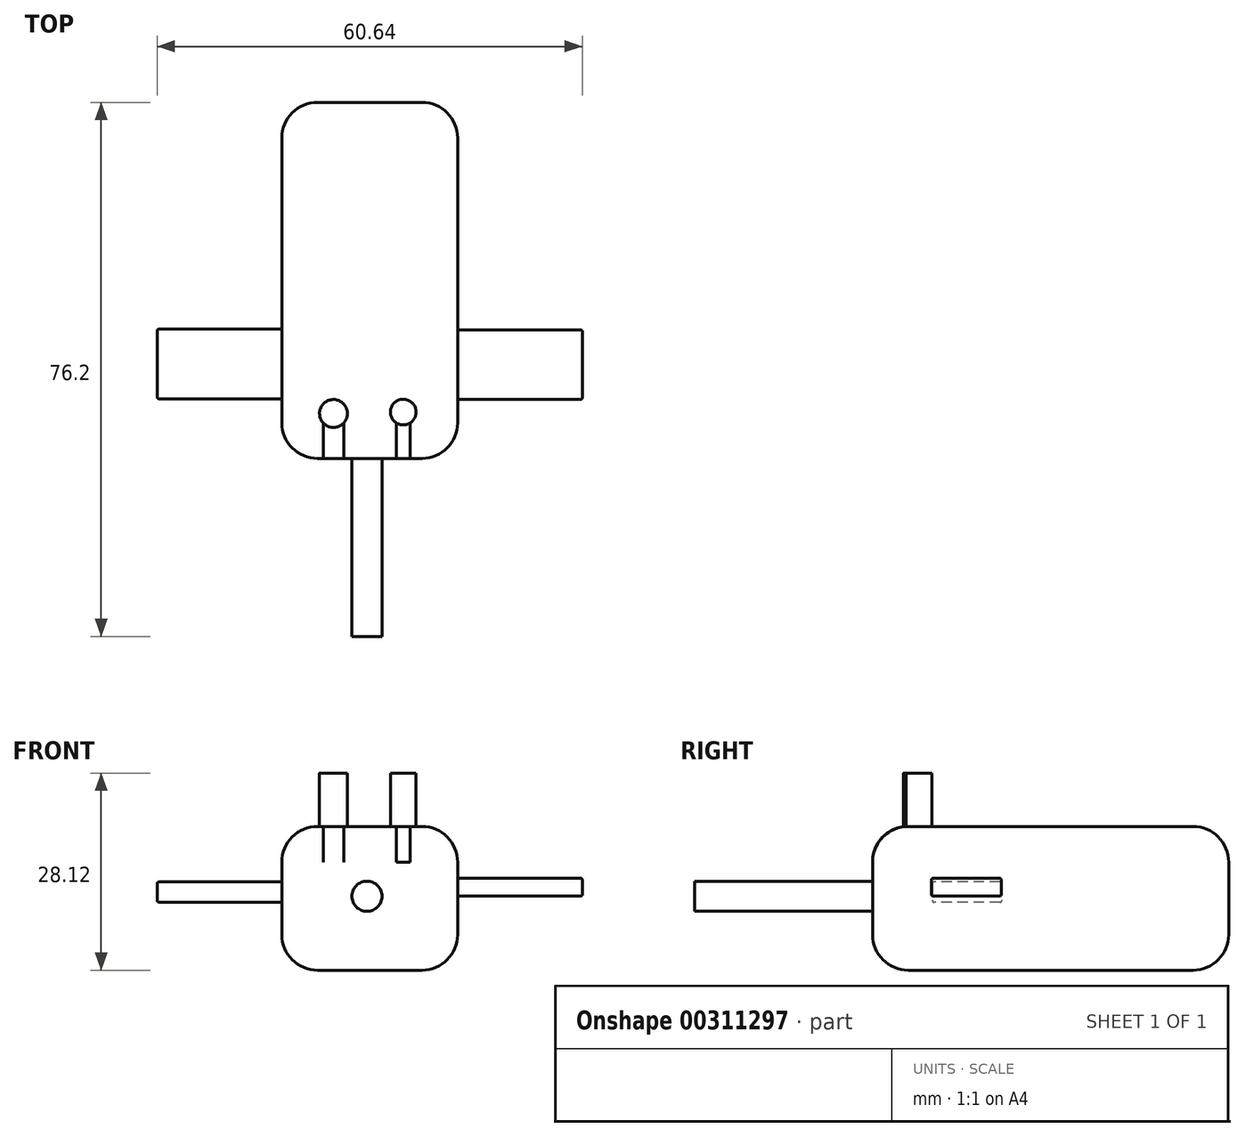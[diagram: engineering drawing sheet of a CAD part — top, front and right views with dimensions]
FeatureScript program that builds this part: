
annotation { "Feature Type Name" : "Feature", "Feature Type Description" : "" }
export const myFeature = defineFeature(function(context is Context, id is Id, definition is map)
    precondition{}
    {
        {
            var Q0;
            Q0=qCreatedBy(makeId("Front.planeOp"),FACE);
            var sketch = newSketch(context, id + "F0", { "sketchPlane" : qUnion([Q0])});
            skLineSegment(sketch, "E0.bottom", {"start": v(-47.37, 39) * mm, "end": v(-22.3, 39) * mm});
            skLineSegment(sketch, "E0.top", {"start": v(-47.37, 18.5) * mm, "end": v(-22.3, 18.5) * mm});
            skLineSegment(sketch, "E0.left", {"start": v(-47.37, 39) * mm, "end": v(-47.37, 18.5) * mm});
            skLineSegment(sketch, "E0.right", {"start": v(-22.3, 39) * mm, "end": v(-22.3, 18.5) * mm});
            skSolve(sketch);
        }
        {
            var Q0;
            Q0=makeQuery(id+"F0.imprint","IMPRINT",FACE,{"disambiguationData":[TD([[makeQuery(id+"F0.imprint","IMPRINT",EDGE,{"derivedFrom":sQuery(id+"F0.wireOp",EDGE,"E0.bottom")}),-1.0]])]});
            extrude(context, id + "F1", {"entities" : qUnion([Q0]), "depth" : 50.8 * mm});
        }
        {
            var Q0;
            Q0=makeQuery(id+"F1.opExtrude","SWEPT_FACE",FACE,{"disambiguationData":[OSD([sQuery(id+"F0.wireOp",EDGE,"E0.right")])]});
            var sketch = newSketch(context, id + "F2", { "sketchPlane" : qUnion([Q0])});
            skLineSegment(sketch, "E1.bottom", {"start": v(-42.4, 31.65) * mm, "end": v(-32.44, 31.65) * mm});
            skLineSegment(sketch, "E1.top", {"start": v(-42.4, 29.06) * mm, "end": v(-32.44, 29.06) * mm});
            skLineSegment(sketch, "E1.left", {"start": v(-42.4, 31.65) * mm, "end": v(-42.4, 29.06) * mm});
            skLineSegment(sketch, "E1.right", {"start": v(-32.44, 31.65) * mm, "end": v(-32.44, 29.06) * mm});
            skSolve(sketch);
        }
        {
            var Q0;
            Q0=makeQuery(id+"F2.imprint","IMPRINT",FACE,{"disambiguationData":[TD([[makeQuery(id+"F2.imprint","IMPRINT",EDGE,{"derivedFrom":sQuery(id+"F2.wireOp",EDGE,"E1.bottom")}),-1.0]])]});
            extrude(context, id + "F3", {"entities" : qUnion([Q0]), "operationType" : NewBodyOperationType.ADD, "depth" : 17.78 * mm});
        }
        {
            var Q0;
            Q0=makeQuery(id+"F1.opExtrude","SWEPT_FACE",FACE,{"disambiguationData":[OSD([sQuery(id+"F0.wireOp",EDGE,"E0.left")])]});
            var sketch = newSketch(context, id + "F4", { "sketchPlane" : qUnion([Q0])});
            skLineSegment(sketch, "E2.bottom", {"start": v(32.34, 31.1) * mm, "end": v(42.3, 31.1) * mm});
            skLineSegment(sketch, "E2.top", {"start": v(32.34, 28.21) * mm, "end": v(42.3, 28.21) * mm});
            skLineSegment(sketch, "E2.left", {"start": v(32.34, 31.1) * mm, "end": v(32.34, 28.21) * mm});
            skLineSegment(sketch, "E2.right", {"start": v(42.3, 31.1) * mm, "end": v(42.3, 28.21) * mm});
            skSolve(sketch);
        }
        {
            var Q0;
            Q0=makeQuery(id+"F4.imprint","IMPRINT",FACE,{"disambiguationData":[TD([[makeQuery(id+"F4.imprint","IMPRINT",EDGE,{"derivedFrom":sQuery(id+"F4.wireOp",EDGE,"E2.bottom")}),-1.0]])]});
            extrude(context, id + "F5", {"entities" : qUnion([Q0]), "operationType" : NewBodyOperationType.ADD, "depth" : 17.78 * mm});
        }
        {
            var Q0;
            Q0=makeQuery(id+"F1.opExtrude","SWEPT_FACE",FACE,{"disambiguationData":[OSD([sQuery(id+"F0.wireOp",EDGE,"E0.bottom")])]});
            var sketch = newSketch(context, id + "F6", { "sketchPlane" : qUnion([Q0])});
            skCircle(sketch, "E3", {"center": v(-40, -44.38) * mm, "radius": 2 * mm});
            skCircle(sketch, "E4", {"center": v(-30.05, -44.18) * mm, "radius": 1.83 * mm});
            skSolve(sketch);
        }
        {
            var Q0;
            Q0=makeQuery(id+"F6.imprint","IMPRINT",FACE,{"disambiguationData":[TD([[makeQuery(id+"F6.imprint","IMPRINT",EDGE,{"derivedFrom":sQuery(id+"F6.wireOp",EDGE,"E3")}),1.0]])]});
            var Q1;
            Q1=makeQuery(id+"F6.imprint","IMPRINT",FACE,{"disambiguationData":[TD([[makeQuery(id+"F6.imprint","IMPRINT",EDGE,{"derivedFrom":sQuery(id+"F6.wireOp",EDGE,"E4")}),1.0]])]});
            extrude(context, id + "F7", {"entities" : qUnion([Q0, Q1]), "operationType" : NewBodyOperationType.ADD, "depth" : 7.62 * mm});
        }
        {
            var Q0;
            Q0=makeQuery(id+"F1.opExtrude","CAP_FACE",FACE,{"disambiguationData":[OSD([sQuery(id+"F0.wireOp",EDGE,"E0.bottom"),sQuery(id+"F0.wireOp",EDGE,"E0.top"),sQuery(id+"F0.wireOp",EDGE,"E0.left"),sQuery(id+"F0.wireOp",EDGE,"E0.right")])],"isStart":false});
            var sketch = newSketch(context, id + "F8", { "sketchPlane" : qUnion([Q0])});
            skCircle(sketch, "E5", {"center": v(-35.23, 29.06) * mm, "radius": 2.14 * mm});
            skSolve(sketch);
        }
        {
            var Q0;
            Q0=makeQuery(id+"F8.imprint","IMPRINT",FACE,{"disambiguationData":[TD([[makeQuery(id+"F8.imprint","IMPRINT",EDGE,{"derivedFrom":sQuery(id+"F8.wireOp",EDGE,"E5")}),1.0]])]});
            extrude(context, id + "F9", {"entities" : qUnion([Q0]), "operationType" : NewBodyOperationType.ADD, "depth" : 25.4 * mm});
        }
        {
            var Q0;
            Q0=makeQuery(id+"F1.opExtrude","SWEPT_EDGE",EDGE,{"disambiguationData":[OSD([sQuery(id+"F0.wireOp",EDGE,"E0.bottom"),sQuery(id+"F0.wireOp",EDGE,"E0.right")])]});
            var Q1;
            Q1=makeQuery(id+"F1.opExtrude","SWEPT_EDGE",EDGE,{"disambiguationData":[OSD([sQuery(id+"F0.wireOp",EDGE,"E0.bottom"),sQuery(id+"F0.wireOp",EDGE,"E0.left")])]});
            var Q2;
            Q2=makeQuery(id+"F1.opExtrude","CAP_EDGE",EDGE,{"disambiguationData":[OSD([sQuery(id+"F0.wireOp",EDGE,"E0.bottom")])],"isStart":true});
            var Q3;
            Q3=makeQuery(id+"F1.opExtrude","SWEPT_EDGE",EDGE,{"disambiguationData":[OSD([sQuery(id+"F0.wireOp",EDGE,"E0.top"),sQuery(id+"F0.wireOp",EDGE,"E0.right")])]});
            var Q4;
            Q4=makeQuery(id+"F1.opExtrude","CAP_EDGE",EDGE,{"disambiguationData":[OSD([sQuery(id+"F0.wireOp",EDGE,"E0.right")])],"isStart":true});
            var Q5;
            Q5=makeQuery(id+"F1.opExtrude","CAP_EDGE",EDGE,{"disambiguationData":[OSD([sQuery(id+"F0.wireOp",EDGE,"E0.right")])],"isStart":false});
            var Q6;
            Q6=makeQuery(id+"F1.opExtrude","CAP_EDGE",EDGE,{"disambiguationData":[OSD([sQuery(id+"F0.wireOp",EDGE,"E0.bottom")])],"isStart":false});
            var Q7;
            Q7=makeQuery(id+"F1.opExtrude","CAP_EDGE",EDGE,{"disambiguationData":[OSD([sQuery(id+"F0.wireOp",EDGE,"E0.left")])],"isStart":false});
            var Q8;
            Q8=makeQuery(id+"F1.opExtrude","CAP_EDGE",EDGE,{"disambiguationData":[OSD([sQuery(id+"F0.wireOp",EDGE,"E0.top")])],"isStart":false});
            var Q9;
            Q9=makeQuery(id+"F1.opExtrude","CAP_EDGE",EDGE,{"disambiguationData":[OSD([sQuery(id+"F0.wireOp",EDGE,"E0.left")])],"isStart":true});
            var Q10;
            Q10=makeQuery(id+"F1.opExtrude","CAP_EDGE",EDGE,{"disambiguationData":[OSD([sQuery(id+"F0.wireOp",EDGE,"E0.top")])],"isStart":true});
            var Q11;
            Q11=makeQuery(id+"F1.opExtrude","SWEPT_EDGE",EDGE,{"disambiguationData":[OSD([sQuery(id+"F0.wireOp",EDGE,"E0.top"),sQuery(id+"F0.wireOp",EDGE,"E0.left")])]});
            fillet(context, id + "F10", {"entities" : qUnion([Q0, Q1, Q2, Q3, Q4, Q5, Q6, Q7, Q8, Q9, Q10, Q11]), "radius" : 5.08 * mm, "tangentPropagation" : true, "allowEdgeOverflow" : false});
        }
        {
            var Q0;
            Q0=makeQuery(id+"F3.opExtrude","SWEPT_EDGE",EDGE,{"disambiguationData":[OSD([sQuery(id+"F2.wireOp",EDGE,"E1.bottom"),sQuery(id+"F2.wireOp",EDGE,"E1.left")])]});
            var Q1;
            Q1=makeQuery(id+"F3.opExtrude","SWEPT_EDGE",EDGE,{"disambiguationData":[OSD([sQuery(id+"F2.wireOp",EDGE,"E1.top"),sQuery(id+"F2.wireOp",EDGE,"E1.left")])]});
            var Q2;
            Q2=makeQuery(id+"F3.opExtrude","CAP_EDGE",EDGE,{"disambiguationData":[OSD([sQuery(id+"F2.wireOp",EDGE,"E1.left")])],"isStart":false});
            var Q3;
            Q3=makeQuery(id+"F5.opExtrude","SWEPT_EDGE",EDGE,{"disambiguationData":[OSD([sQuery(id+"F4.wireOp",EDGE,"E2.bottom"),sQuery(id+"F4.wireOp",EDGE,"E2.right")])]});
            var Q4;
            Q4=makeQuery(id+"F5.opExtrude","SWEPT_EDGE",EDGE,{"disambiguationData":[OSD([sQuery(id+"F4.wireOp",EDGE,"E2.top"),sQuery(id+"F4.wireOp",EDGE,"E2.right")])]});
            var Q5;
            Q5=makeQuery(id+"F5.opExtrude","CAP_EDGE",EDGE,{"disambiguationData":[OSD([sQuery(id+"F4.wireOp",EDGE,"E2.right")])],"isStart":false});
            var Q6;
            Q6=makeQuery(id+"F5.opExtrude","CAP_EDGE",EDGE,{"disambiguationData":[OSD([sQuery(id+"F4.wireOp",EDGE,"E2.left")])],"isStart":false});
            var Q7;
            Q7=makeQuery(id+"F5.opExtrude","CAP_EDGE",EDGE,{"disambiguationData":[OSD([sQuery(id+"F4.wireOp",EDGE,"E2.top")])],"isStart":false});
            var Q8;
            Q8=makeQuery(id+"F5.opExtrude","CAP_EDGE",EDGE,{"disambiguationData":[OSD([sQuery(id+"F4.wireOp",EDGE,"E2.bottom")])],"isStart":false});
            var Q9;
            Q9=makeQuery(id+"F5.opExtrude","SWEPT_EDGE",EDGE,{"disambiguationData":[OSD([sQuery(id+"F4.wireOp",EDGE,"E2.bottom"),sQuery(id+"F4.wireOp",EDGE,"E2.left")])]});
            var Q10;
            Q10=makeQuery(id+"F5.opExtrude","SWEPT_EDGE",EDGE,{"disambiguationData":[OSD([sQuery(id+"F4.wireOp",EDGE,"E2.top"),sQuery(id+"F4.wireOp",EDGE,"E2.left")])]});
            var Q11;
            Q11=makeQuery(id+"F3.opExtrude","CAP_EDGE",EDGE,{"disambiguationData":[OSD([sQuery(id+"F2.wireOp",EDGE,"E1.bottom")])],"isStart":false});
            var Q12;
            Q12=makeQuery(id+"F3.opExtrude","CAP_EDGE",EDGE,{"disambiguationData":[OSD([sQuery(id+"F2.wireOp",EDGE,"E1.top")])],"isStart":false});
            var Q13;
            Q13=makeQuery(id+"F3.opExtrude","SWEPT_EDGE",EDGE,{"disambiguationData":[OSD([sQuery(id+"F2.wireOp",EDGE,"E1.top"),sQuery(id+"F2.wireOp",EDGE,"E1.right")])]});
            var Q14;
            Q14=makeQuery(id+"F3.opExtrude","CAP_EDGE",EDGE,{"disambiguationData":[OSD([sQuery(id+"F2.wireOp",EDGE,"E1.right")])],"isStart":false});
            var Q15;
            Q15=makeQuery(id+"F3.opExtrude","SWEPT_EDGE",EDGE,{"disambiguationData":[OSD([sQuery(id+"F2.wireOp",EDGE,"E1.bottom"),sQuery(id+"F2.wireOp",EDGE,"E1.right")])]});
            fillet(context, id + "F11", {"entities" : qUnion([Q0, Q1, Q2, Q3, Q4, Q5, Q6, Q7, Q8, Q9, Q10, Q11, Q12, Q13, Q14, Q15]), "radius" : 0.25 * mm, "tangentPropagation" : true, "allowEdgeOverflow" : false});
        }
    });
